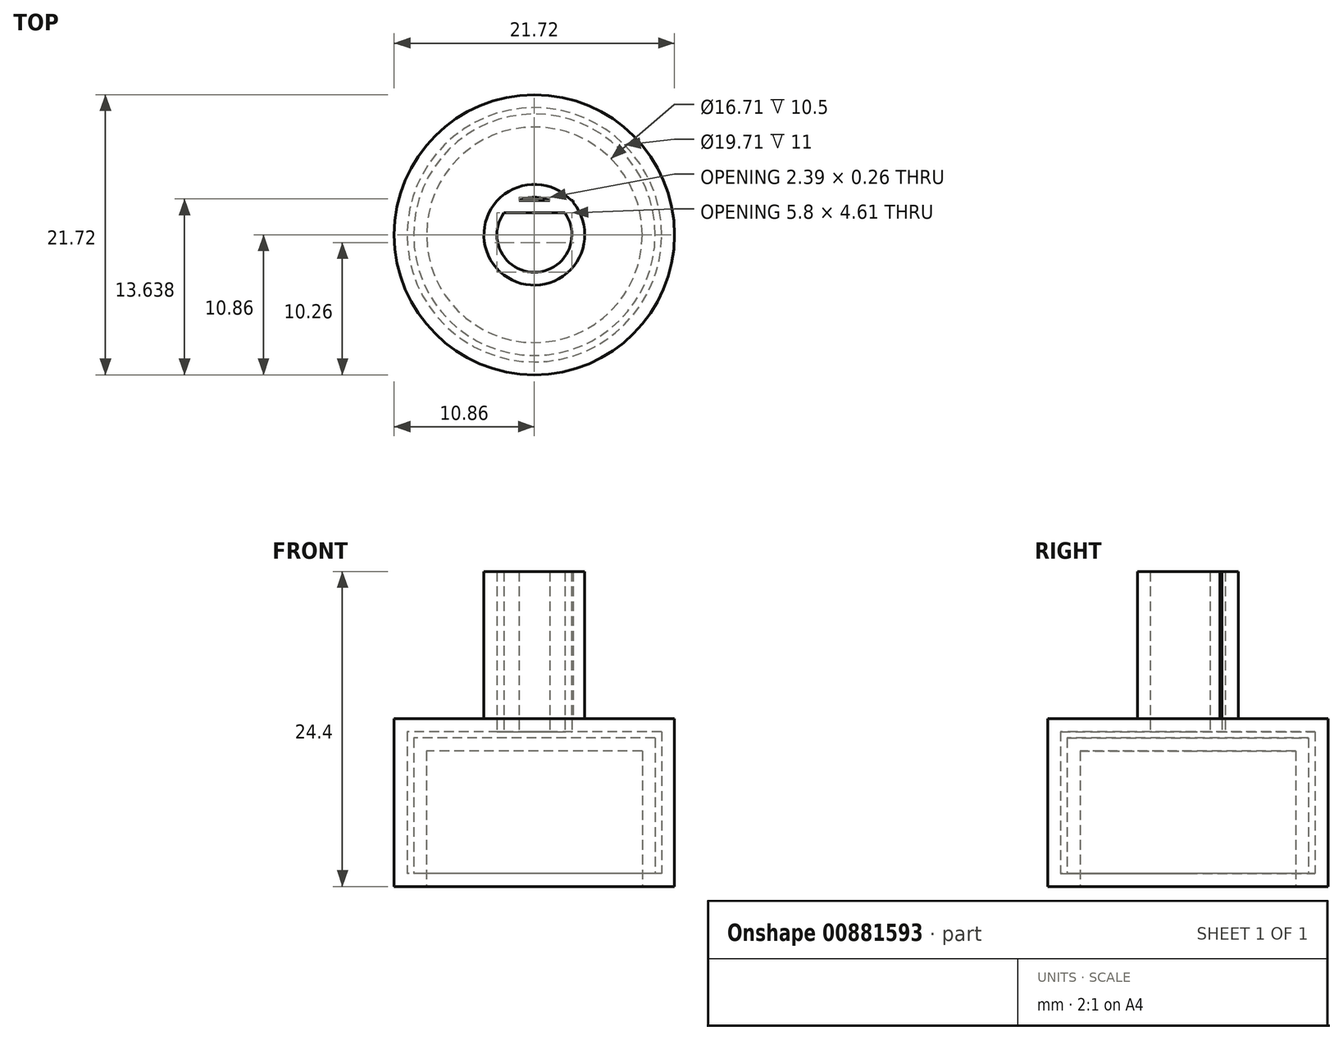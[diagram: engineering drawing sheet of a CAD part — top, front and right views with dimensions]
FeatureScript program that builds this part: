
annotation { "Feature Type Name" : "Feature", "Feature Type Description" : "" }
export const myFeature = defineFeature(function(context is Context, id is Id, definition is map)
    precondition{}
    {
        {
            var Q0;
            Q0=qCreatedBy(makeId("Top.planeOp"),FACE);
            var sketch = newSketch(context, id + "F0", { "sketchPlane" : qUnion([Q0])});
            skCircle(sketch, "E0", {"center": v(0, 0) * mm, "radius": 10.86 * mm});
            skSolve(sketch);
        }
        {
            var Q0;
            Q0=qSketchRegion(id+"F0",true);
            extrude(context, id + "F1", {"entities" : qUnion([Q0]), "depth" : 13 * mm, "offsetDistance" : 25 * mm});
        }
        {
            var Q0;
            Q0=makeQuery(id+"F1.opExtrude","CAP_FACE",FACE,{"disambiguationData":[OSD([sQuery(id+"F0.wireOp",EDGE,"E0")])],"isStart":true});
            shell(context, id + "F2", {"entities" : qUnion([Q0]), "thickness" : 2.5 * mm});
        }
        {
            var Q0;
            Q0=makeQuery(id+"F1.opExtrude","CAP_FACE",FACE,{"disambiguationData":[OSD([sQuery(id+"F0.wireOp",EDGE,"E0")])],"isStart":false});
            var sketch = newSketch(context, id + "F3", { "sketchPlane" : qUnion([Q0])});
            skCircle(sketch, "E1", {"center": v(0, 0) * mm, "radius": 3.9 * mm});
            skSolve(sketch);
        }
        {
            var Q0;
            Q0=qSketchRegion(id+"F3",true);
            extrude(context, id + "F4", {"entities" : qUnion([Q0]), "operationType" : NewBodyOperationType.ADD, "depth" : 11.4 * mm, "offsetDistance" : 25 * mm});
        }
        {
            var Q0;
            Q0=makeQuery(id+"F4.opExtrude","CAP_FACE",FACE,{"disambiguationData":[OSD([sQuery(id+"F3.wireOp",EDGE,"E1")])],"isStart":false});
            shell(context, id + "F5", {"entities" : qUnion([Q0]), "thickness" : 1 * mm});
        }
        {
            var Q0;
            Q0=makeQuery(id+"F4.opExtrude","CAP_FACE",FACE,{"disambiguationData":[OSD([sQuery(id+"F3.wireOp",EDGE,"E1")])],"isStart":false});
            var sketch = newSketch(context, id + "F6", { "sketchPlane" : qUnion([Q0])});
            skLineSegment(sketch, "E2.bottom", {"start": v(-2.87, 2.65) * mm, "end": v(3, 2.65) * mm});
            skLineSegment(sketch, "E2.top", {"start": v(-2.87, 1.7) * mm, "end": v(3, 1.7) * mm});
            skLineSegment(sketch, "E2.left", {"start": v(-2.87, 2.65) * mm, "end": v(-2.87, 1.7) * mm});
            skLineSegment(sketch, "E2.right", {"start": v(3, 2.65) * mm, "end": v(3, 1.7) * mm});
            skSolve(sketch);
        }
        {
            var Q0;
            Q0=qSketchRegion(id+"F6",true);
            extrude(context, id + "F7", {"entities" : qUnion([Q0]), "operationType" : NewBodyOperationType.ADD, "oppositeDirection" : true, "depth" : 12.4 * mm, "offsetDistance" : 25 * mm});
        }
    });
